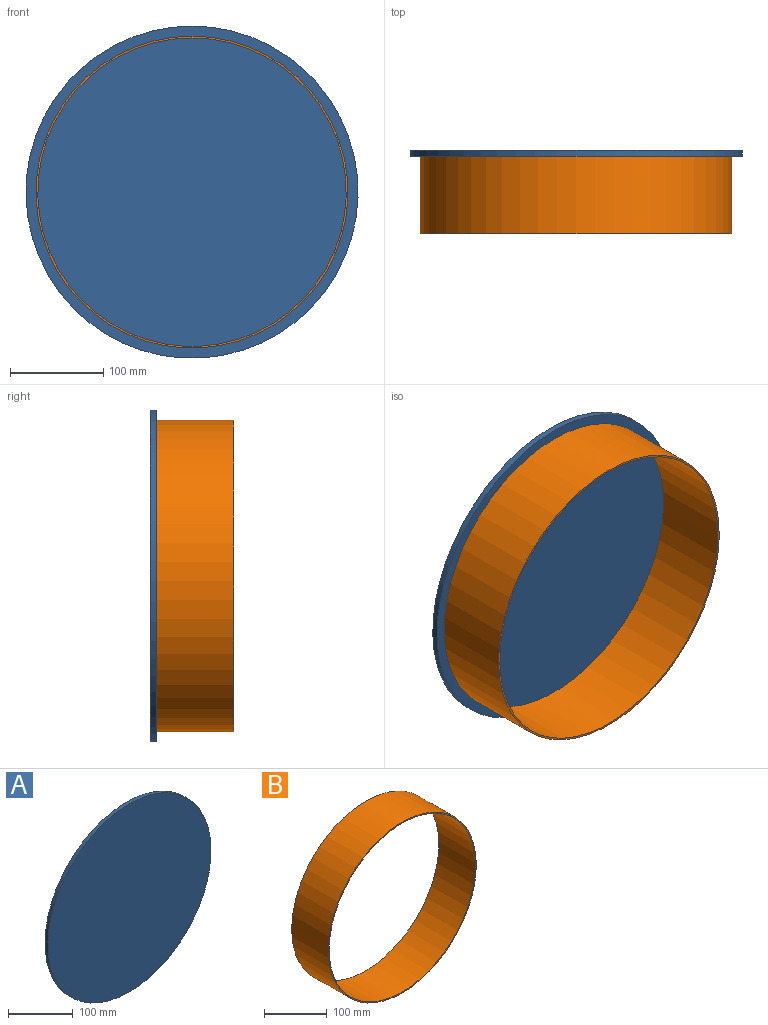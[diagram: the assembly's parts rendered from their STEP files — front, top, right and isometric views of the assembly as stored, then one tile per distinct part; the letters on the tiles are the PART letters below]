
ASSEMBLY  parts=2 mates=1
PART A: 3 faces, bbox 355.6x6.4x355.6 mm
  f0: cylinder r=177.8mm len=355.6mm, axis (0,1,0), area 7093.9mm2, adj f1,f2
  f1: plane 355.6x355.6mm, normal (0,-1,0), area 99314.7mm2, adj f0
  f2: plane 355.6x355.6mm, normal (0,1,0), area 99314.7mm2, adj f0
PART B: 4 faces, bbox 334x82.6x334 mm
  f0: cylinder r=165.1mm len=330.2mm, axis (0,1,0), area 85633.6mm2, adj f2,f3
  f1: cylinder r=167mm len=333.99mm, axis (0,1,0), area 86617.7mm2, adj f2,f3
  f2: plane 333.99x333.99mm, normal (0,-1,0), area 1979.6mm2, adj f0,f1
  f3: plane 333.99x333.99mm, normal (0,1,0), area 1979.6mm2, adj f0,f1
PLACE A rot(axis=(1,0,0),180deg) t=(0,-165.1,0)mm
PLACE B rot(axis=(1,0,0),180deg) t=(0,-165.1,0)mm
MATE fastened B.f0 <-> A.f0  axis (0,1,0) through (0,-82.55,0)mm
